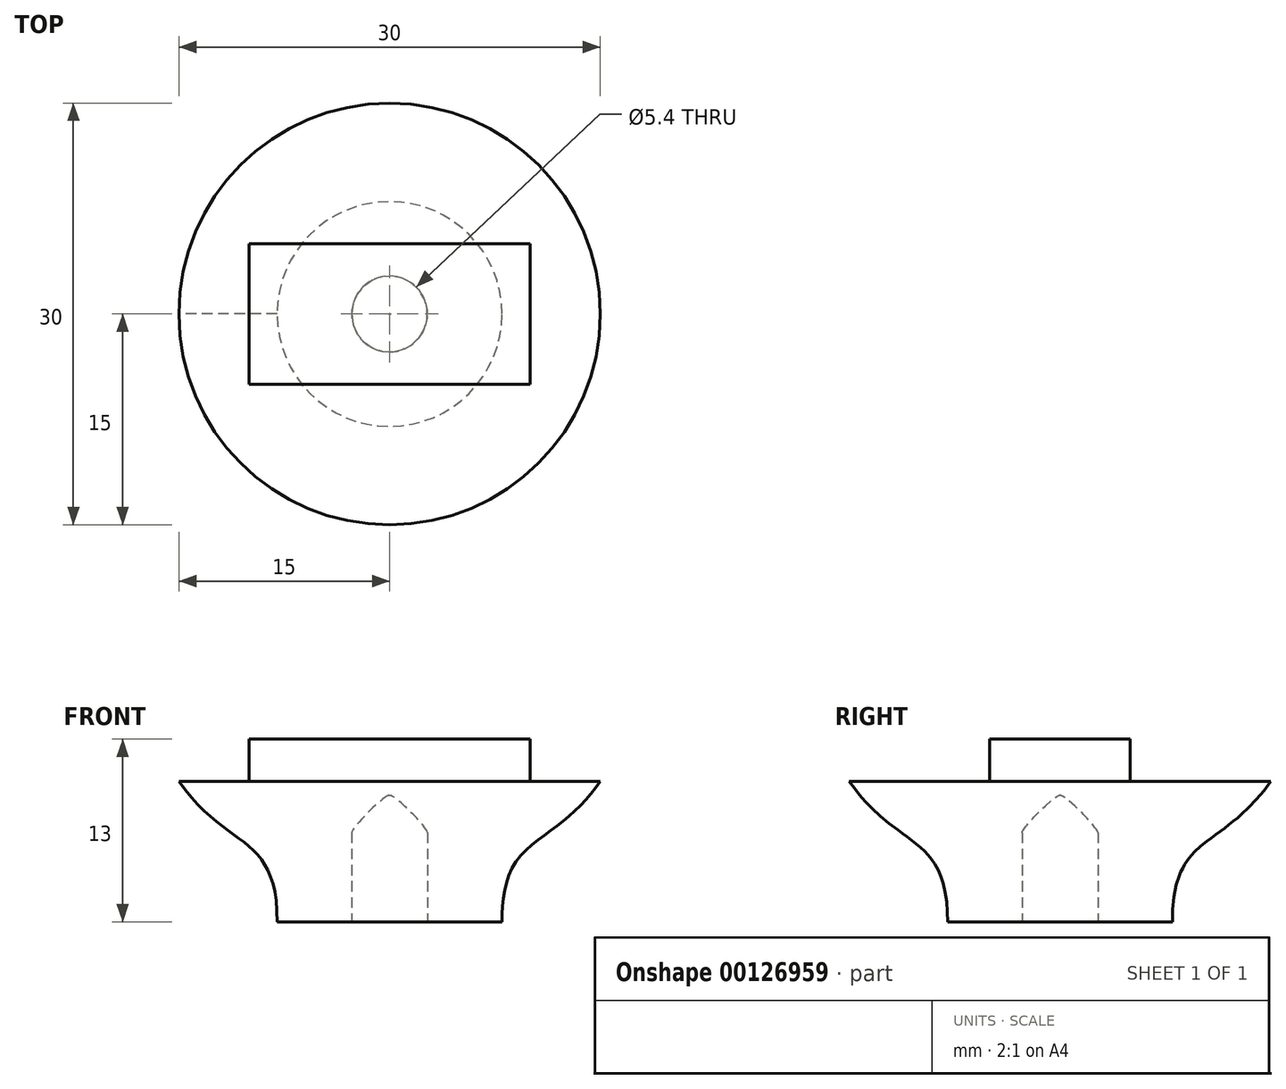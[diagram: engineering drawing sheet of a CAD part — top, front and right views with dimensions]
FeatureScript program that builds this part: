
annotation { "Feature Type Name" : "Feature", "Feature Type Description" : "" }
export const myFeature = defineFeature(function(context is Context, id is Id, definition is map)
    precondition{}
    {
        {
            var Q0;
            Q0=qCreatedBy(makeId("Front.planeOp"),FACE);
            var sketch = newSketch(context, id + "F0", { "sketchPlane" : qUnion([Q0])});
            skLineSegment(sketch, "E0", {"start": v(0, 0) * mm, "end": v(-2.7, 0) * mm});
            skLineSegment(sketch, "E1", {"start": v(-2.7, 0) * mm, "end": v(-2.7, -9) * mm});
            skLineSegment(sketch, "E2", {"start": v(-2.7, -9) * mm, "end": v(-8, -9) * mm});
            skLineSegment(sketch, "E3", {"start": v(-8, -9) * mm, "end": v(-15, 1) * mm, "construction": true});
            skLineSegment(sketch, "E4", {"start": v(-15, 1) * mm, "end": v(0, 1) * mm});
            skLineSegment(sketch, "E5", {"start": v(0, 0) * mm, "end": v(0, 1) * mm});
            skLineSegment(sketch, "E6", {"start": v(0, -25) * mm, "end": v(0, 25) * mm, "construction": true});
            skFitSpline(sketch, "E7", {"points": [v(-8, -9) * mm, v(-15, 1) * mm], "startDerivative": vector(0, 19.14) * mm, "endDerivative": vector(-10.5, 15) * mm});
            skSolve(sketch);
        }
        {
            var Q0;
            Q0 = qSketchRegion(id + "F0", true);
            var Q1;
            Q1=sQuery(id+"F0.wireOp",EDGE,"E6");
            revolve(context, id + "F1", {"entities" : qUnion([Q0]), "axis" : qUnion([Q1]), "revolveType" : RevolveType.FULL});
        }
        {
            var Q0;
            Q0=makeQuery(id+"F1.opRevolve","SWEPT_FACE",FACE,{"disambiguationData":[OSD([sQuery(id+"F0.wireOp",EDGE,"E4")])]});
            var sketch = newSketch(context, id + "F2", { "sketchPlane" : qUnion([Q0])});
            skLineSegment(sketch, "E8.bottom", {"start": v(-10, 5) * mm, "end": v(10, 5) * mm});
            skLineSegment(sketch, "E8.top", {"start": v(-10, -5) * mm, "end": v(10, -5) * mm});
            skLineSegment(sketch, "E8.left", {"start": v(-10, 5) * mm, "end": v(-10, -5) * mm});
            skLineSegment(sketch, "E8.right", {"start": v(10, 5) * mm, "end": v(10, -5) * mm});
            skPoint(sketch, "E8.middle", {"position": v(0, 0) * mm});
            skSolve(sketch);
        }
        {
            var Q0;
            Q0 = qSketchRegion(id + "F2", true);
            extrude(context, id + "F3", {"entities" : qUnion([Q0]), "operationType" : NewBodyOperationType.ADD, "depth" : 3 * mm});
        }
        {
            var Q0;
            Q0=makeQuery(id+"F1.opRevolve","SWEPT_FACE",FACE,{"disambiguationData":[OSD([sQuery(id+"F0.wireOp",EDGE,"E0")])]});
            fillet(context, id + "F4", {"entities" : qUnion([Q0]), "radius" : 2.65 * mm, "tangentPropagation" : true, "rho" : .1, "crossSection" : FilletCrossSection.CONIC, "allowEdgeOverflow" : false});
        }
    });
